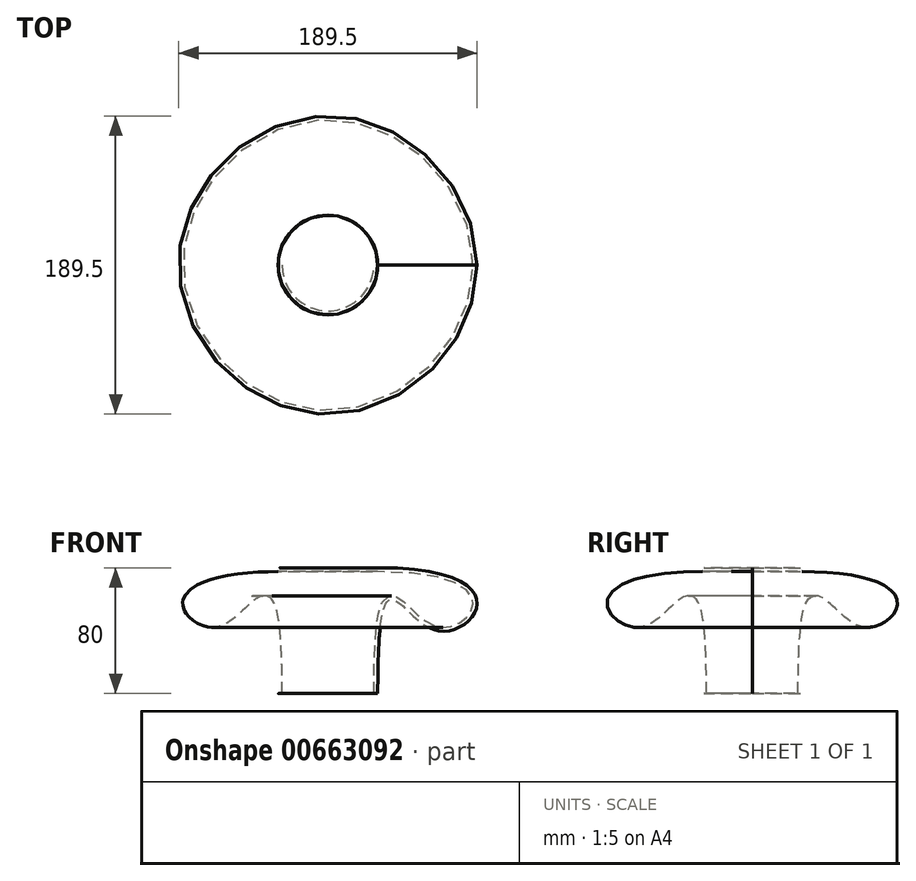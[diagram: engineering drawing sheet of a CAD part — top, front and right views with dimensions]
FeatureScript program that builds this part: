
annotation { "Feature Type Name" : "Feature", "Feature Type Description" : "" }
export const myFeature = defineFeature(function(context is Context, id is Id, definition is map)
    precondition{}
    {
        {
            var Q0;
            Q0=qCreatedBy(makeId("Top.planeOp"),FACE);
            cPlane(context, id + "F0", {"entities" : qUnion([Q0]), "cplaneType" : CPlaneType.OFFSET, "offset" : 40 * mm, "width" : 150 * mm, "height" : 150 * mm});
        }
        {
            var Q0;
            Q0=qCreatedBy(makeId("Top.planeOp"),FACE);
            cPlane(context, id + "F1", {"entities" : qUnion([Q0]), "cplaneType" : CPlaneType.OFFSET, "offset" : 80 * mm, "width" : 150 * mm, "height" : 150 * mm});
        }
        {
            var Q0;
            Q0=qCreatedBy(makeId("Top.planeOp"),FACE);
            var sketch = newSketch(context, id + "F2", { "sketchPlane" : qUnion([Q0])});
            skCircle(sketch, "E0", {"center": v(0, 0) * mm, "radius": 31.63 * mm});
            skSolve(sketch);
        }
        {
            var Q0;
            Q0=qCreatedBy(id+"F0.planeOp",FACE);
            var sketch = newSketch(context, id + "F3", { "sketchPlane" : qUnion([Q0])});
            skCircle(sketch, "E1", {"center": v(0, 0) * mm, "radius": 69.37 * mm});
            skSolve(sketch);
        }
        {
            var Q0;
            Q0=qCreatedBy(id+"F1.planeOp",FACE);
            var sketch = newSketch(context, id + "F4", { "sketchPlane" : qUnion([Q0])});
            skCircle(sketch, "E2.0", {"center": v(0, 0) * mm, "radius": 31.63 * mm});
            skSolve(sketch);
        }
        {
            var Q0;
            Q0=makeQuery(id+"F2.imprint","IMPRINT",FACE,{"disambiguationData":[TD([[makeQuery(id+"F2.imprint","IMPRINT",EDGE,{"derivedFrom":sQuery(id+"F2.wireOp",EDGE,"E0")}),1.0]])]});
            var Q1;
            Q1=makeQuery(id+"F3.imprint","IMPRINT",FACE,{"disambiguationData":[TD([[makeQuery(id+"F3.imprint","IMPRINT",EDGE,{"derivedFrom":sQuery(id+"F3.wireOp",EDGE,"E1")}),1.0]])]});
            var Q2;
            Q2=makeQuery(id+"F4.imprint","IMPRINT",FACE,{"disambiguationData":[TD([[makeQuery(id+"F4.imprint","IMPRINT",EDGE,{"derivedFrom":sQuery(id+"F4.wireOp",EDGE,"E2.0")}),1.0]])]});
            loft(context, id + "F5", {"startCondition" : LoftEndDerivativeType.NORMAL_TO_PROFILE, "startMagnitude" : 7, "endCondition" : LoftEndDerivativeType.TANGENT_TO_PROFILE, "endMagnitude" : 5, "sheetProfilesArray" : [{ "sheetProfileEntities" : qUnion([Q0]) }, { "sheetProfileEntities" : qUnion([Q1]) }, { "sheetProfileEntities" : qUnion([Q2]) }]});
        }
        {
            var Q0;
            Q0=makeQuery(id+"F5.opLoft","CAP_FACE",FACE,{"disambiguationData":[OSD([makeQuery(id+"F2.imprint","IMPRINT",FACE,{"disambiguationData":[TD([[makeQuery(id+"F2.imprint","IMPRINT",EDGE,{"derivedFrom":sQuery(id+"F2.wireOp",EDGE,"E0")}),1.0]])]})])],"isStart":true});
            shell(context, id + "F6", {"entities" : qUnion([Q0]), "thickness" : 2.5 * mm});
        }
    });
